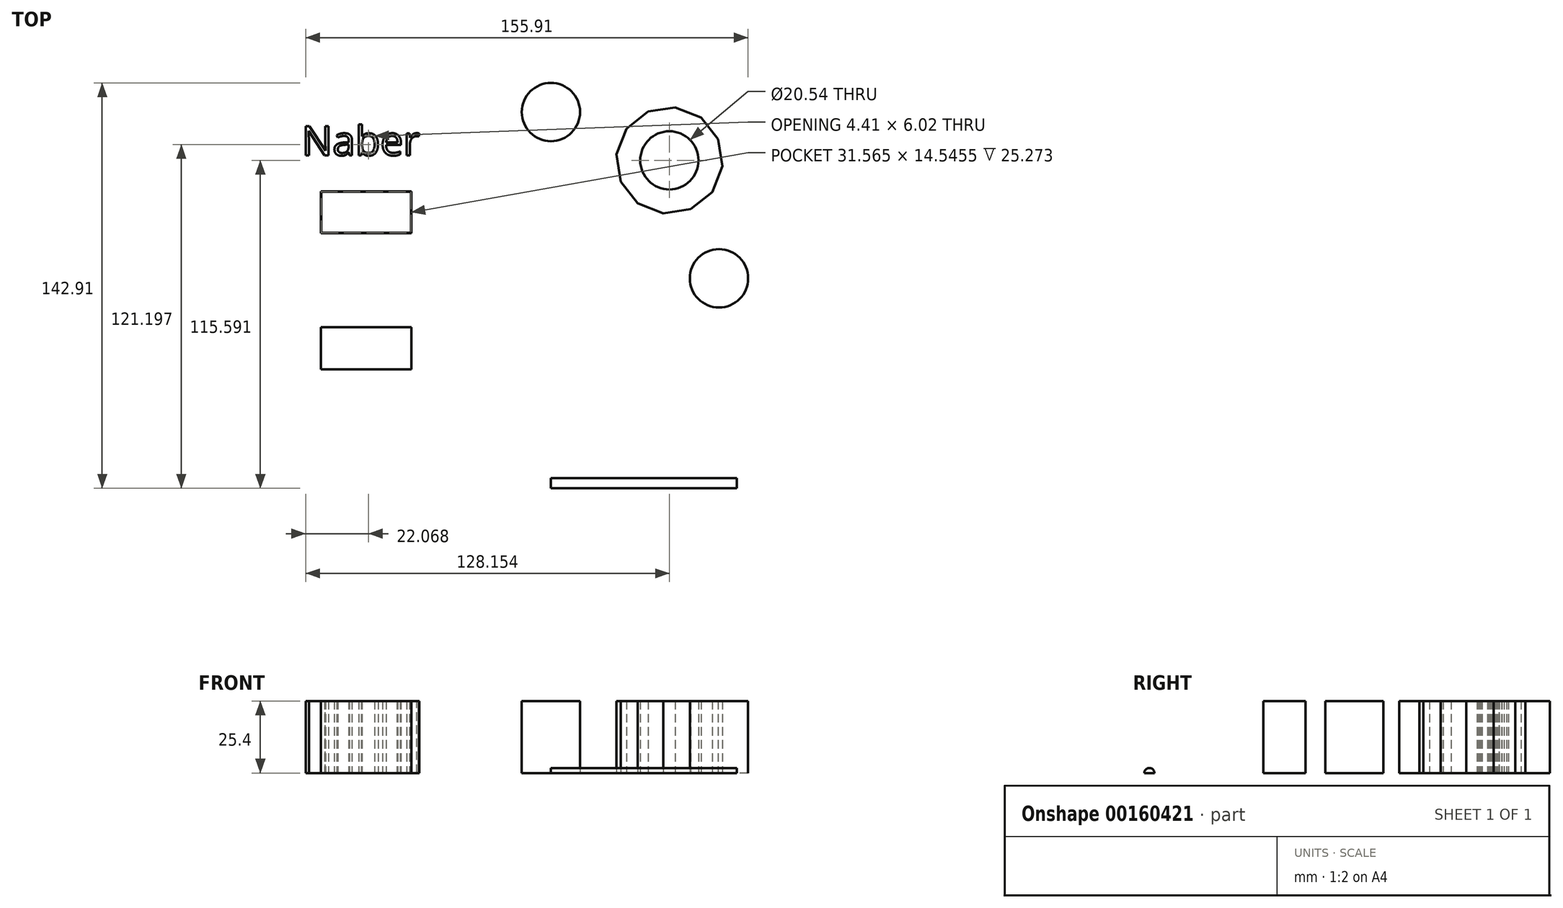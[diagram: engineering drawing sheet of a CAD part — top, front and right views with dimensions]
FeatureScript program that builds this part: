
annotation { "Feature Type Name" : "Feature", "Feature Type Description" : "" }
export const myFeature = defineFeature(function(context is Context, id is Id, definition is map)
    precondition{}
    {
        {
            var Q0;
            Q0=qCreatedBy(makeId("Top.planeOp"),FACE);
            var sketch = newSketch(context, id + "F0", { "sketchPlane" : qUnion([Q0])});
            skLineSegment(sketch, "E0.bottom", {"start": v(-28.24, 19.15) * mm, "end": v(21.4, 19.15) * mm});
            skLineSegment(sketch, "E0.left", {"start": v(-34.6, 12.8) * mm, "end": v(-34.6, -10.57) * mm, "construction": true});
            skLineSegment(sketch, "E0.right", {"start": v(27.75, 12.8) * mm, "end": v(27.75, -10.82) * mm});
            skLineSegment(sketch, "E1", {"start": v(-45.2, 20.32) * mm, "end": v(-7.57, 52.79) * mm});
            skLineSegment(sketch, "E2.bottom", {"start": v(-49.2, -31.36) * mm, "end": v(-81.03, -31.36) * mm});
            skLineSegment(sketch, "E2.top", {"start": v(-49.2, -16.56) * mm, "end": v(-81.03, -16.56) * mm});
            skLineSegment(sketch, "E2.left", {"start": v(-49.2, -31.36) * mm, "end": v(-49.2, -16.56) * mm});
            skLineSegment(sketch, "E2.right", {"start": v(-81.03, -31.36) * mm, "end": v(-81.03, -16.56) * mm});
            skPoint(sketch, "E2.middle", {"position": v(-65.12, -23.96) * mm});
            skCircle(sketch, "E3.cCircle", {"center": v(0, -36.17) * mm, "radius": 24.44 * mm, "construction": true});
            skLineSegment(sketch, "E3.0", {"start": v(24.24, -42.95) * mm, "end": v(18.31, -53.43) * mm});
            skLineSegment(sketch, "E3.1", {"start": v(18.31, -53.43) * mm, "end": v(8.19, -59.97) * mm});
            skLineSegment(sketch, "E3.2", {"start": v(8.19, -59.97) * mm, "end": v(-3.8, -61.05) * mm});
            skLineSegment(sketch, "E3.3", {"start": v(-3.8, -61.05) * mm, "end": v(-14.94, -56.42) * mm});
            skLineSegment(sketch, "E3.4", {"start": v(-14.94, -56.42) * mm, "end": v(-22.64, -47.16) * mm});
            skLineSegment(sketch, "E3.5", {"start": v(-22.64, -47.16) * mm, "end": v(-25.16, -35.38) * mm});
            skLineSegment(sketch, "E3.6", {"start": v(-25.16, -35.38) * mm, "end": v(-21.91, -23.78) * mm});
            skLineSegment(sketch, "E3.7", {"start": v(-21.91, -23.78) * mm, "end": v(-13.65, -15.02) * mm});
            skLineSegment(sketch, "E3.8", {"start": v(-13.65, -15.02) * mm, "end": v(-2.25, -11.1) * mm});
            skLineSegment(sketch, "E3.9", {"start": v(-2.25, -11.1) * mm, "end": v(9.65, -12.92) * mm});
            skLineSegment(sketch, "E3.11", {"start": v(19.35, -20.07) * mm, "end": v(24.61, -30.9) * mm});
            skLineSegment(sketch, "E3.12", {"start": v(24.61, -30.9) * mm, "end": v(24.24, -42.95) * mm});
            skPoint(sketch, "E3.0.midPoint", {"position": v(21.27, -48.2) * mm});
            skCircle(sketch, "E4.cCircle", {"center": v(41.76, 42.27) * mm, "radius": 18.76 * mm, "construction": true});
            skLineSegment(sketch, "E4.0", {"start": v(58.96, 49.77) * mm, "end": v(60.4, 40.17) * mm});
            skLineSegment(sketch, "E4.1", {"start": v(60.4, 40.17) * mm, "end": v(56.86, 31.13) * mm});
            skLineSegment(sketch, "E4.2", {"start": v(56.86, 31.13) * mm, "end": v(49.26, 25.07) * mm});
            skLineSegment(sketch, "E4.3", {"start": v(49.26, 25.07) * mm, "end": v(39.66, 23.63) * mm});
            skLineSegment(sketch, "E4.4", {"start": v(39.66, 23.63) * mm, "end": v(30.62, 27.18) * mm});
            skLineSegment(sketch, "E4.5", {"start": v(30.62, 27.18) * mm, "end": v(24.57, 34.77) * mm});
            skLineSegment(sketch, "E4.6", {"start": v(24.57, 34.77) * mm, "end": v(23.12, 44.37) * mm});
            skLineSegment(sketch, "E4.7", {"start": v(23.12, 44.37) * mm, "end": v(26.67, 53.41) * mm});
            skLineSegment(sketch, "E4.8", {"start": v(26.67, 53.41) * mm, "end": v(34.26, 59.47) * mm});
            skLineSegment(sketch, "E4.9", {"start": v(34.26, 59.47) * mm, "end": v(43.87, 60.91) * mm});
            skLineSegment(sketch, "E4.10", {"start": v(43.87, 60.91) * mm, "end": v(52.9, 57.36) * mm});
            skLineSegment(sketch, "E4.11", {"start": v(52.9, 57.36) * mm, "end": v(58.96, 49.77) * mm});
            skPoint(sketch, "E5", {"position": v(0, 19.15) * mm});
            skText(sketch, "E6", { "text": "Naber", "fontName": "OpenSans-Regular.ttf"});
            skPoint(sketch, "E7.visualSharp", {"position": v(-34.6, 19.15) * mm});
            skArc(sketch, "E7.filletArc", {"start": v(-28.24, 19.15) * mm, "mid": v(-32.73, 17.29) * mm, "end": v(-34.6, 12.8) * mm, "construction": true});
            skPoint(sketch, "E8.visualSharp", {"position": v(27.75, 19.15) * mm});
            skArc(sketch, "E8.filletArc", {"start": v(27.75, 12.8) * mm, "mid": v(25.89, 17.29) * mm, "end": v(21.4, 19.15) * mm});
            skLineSegment(sketch, "E9", {"start": v(-34.6, -10.57) * mm, "end": v(-34.6, -10.82) * mm, "construction": true});
            skLineSegment(sketch, "E10.0", {"start": v(-34.38, -12.02) * mm, "end": v(-26.12, -3.25) * mm});
            skLineSegment(sketch, "E11.0", {"start": v(53.62, -3.42) * mm, "end": v(58.88, -14.26) * mm});
            skLineSegment(sketch, "E12.MirrorCS", {"start": v(-49.2, 16.56) * mm, "end": v(-81.03, 16.56) * mm});
            skLineSegment(sketch, "E13.MirrorCS", {"start": v(-49.2, 31.36) * mm, "end": v(-49.2, 16.56) * mm});
            skLineSegment(sketch, "E14.MirrorCS", {"start": v(-49.2, 31.36) * mm, "end": v(-81.03, 31.36) * mm});
            skLineSegment(sketch, "E15.MirrorCS", {"start": v(-81.03, 31.36) * mm, "end": v(-81.03, 16.56) * mm});
            skCircle(sketch, "E16", {"center": v(0, 59.31) * mm, "radius": 10.27 * mm});
            skCircle(sketch, "E17.1.0", {"center": v(41.76, 42.27) * mm, "radius": 10.27 * mm});
            skCircle(sketch, "E17.2.0", {"center": v(59.24, 0.69) * mm, "radius": 10.27 * mm});
            skPoint(sketch, "E17.center", {"position": v(0.3, 0.38) * mm});
            skLineSegment(sketch, "E17.anchor1", {"start": v(0.3, 0.38) * mm, "end": v(0, 59.31) * mm, "construction": true});
            skLineSegment(sketch, "E17.anchor2", {"start": v(0.3, 0.38) * mm, "end": v(59.24, 0.69) * mm, "construction": true});
            skLineSegment(sketch, "E18", {"start": v(-49.2, 31) * mm, "end": v(-49.2, 2.1) * mm});
            skPoint(sketch, "E19", {"position": v(-49.4, -50.08) * mm});
            skLineSegment(sketch, "E20", {"start": v(0, -71.54) * mm, "end": v(65.54, -71.54) * mm});
            const initialGuessF0  = {"E6": [-0.0878, 0.04403, 1, 0, 0.01037]};
            skSetInitialGuess(sketch, initialGuessF0);
            skSolve(sketch);
        }
        {
            var Q0;
            Q0=qCreatedBy(makeId("Right.planeOp"),FACE);
            var sketch = newSketch(context, id + "F1", { "sketchPlane" : qUnion([Q0])});
            skPoint(sketch, "E21.0", {"position": v(-71.54, 0) * mm});
            skArc(sketch, "E22", {"start": v(-69.76, 0) * mm, "mid": v(-71.54, 1.78) * mm, "end": v(-73.32, 0) * mm});
            skLineSegment(sketch, "E23", {"start": v(-73.78, 0) * mm, "end": v(-69.07, 0) * mm});
            skSolve(sketch);
        }
        {
            var Q0;
            {var subQ0=sQuery(id+"F1.wireOp",EDGE,"E22");Q0=makeQuery(id+"F1.imprint","IMPRINT",FACE,{"disambiguationData":[TD([[makeQuery(id+"F1.imprint","IMPRINT",EDGE,{"derivedFrom":subQ0}),1.0]])]});}
            var Q1;
            Q1=sQuery(id+"F0.wireOp",EDGE,"E20");
            sweep(context, id + "F2", {"profiles" : qUnion([Q0]), "path" : qUnion([Q1])});
        }
        {
            var Q0;
            Q0 = qSketchRegion(id + "F0", true);
            extrude(context, id + "F3", {"entities" : qUnion([Q0]), "depth" : 25.4 * mm});
        }
        {
            var Q0;
            Q0=makeQuery(id+"F3.opExtrude","CAP_FACE",FACE,{"disambiguationData":[OSD([sQuery(id+"F0.wireOp",EDGE,"E13.MirrorCS"),sQuery(id+"F0.wireOp",EDGE,"E14.MirrorCS"),sQuery(id+"F0.wireOp",EDGE,"E15.MirrorCS"),sQuery(id+"F0.wireOp",EDGE,"E12.MirrorCS"),sQuery(id+"F0.wireOp",EDGE,"E18")])],"isStart":false});
            shell(context, id + "F4", {"entities" : qUnion([Q0]), "thickness" : 0.13 * mm});
        }
    });
